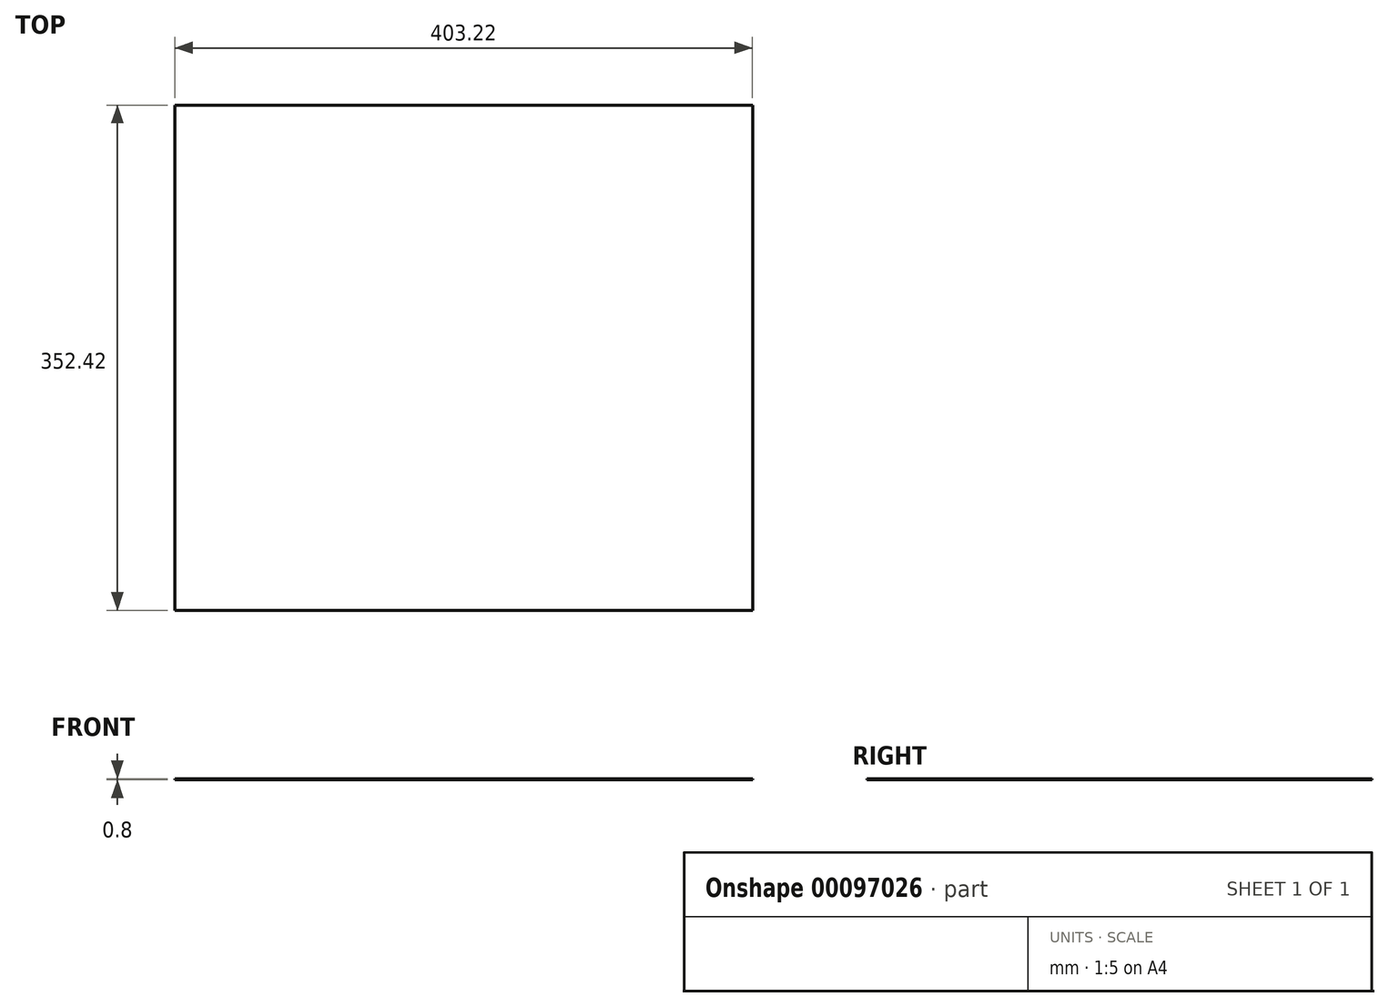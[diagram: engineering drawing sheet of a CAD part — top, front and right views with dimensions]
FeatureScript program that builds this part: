
annotation { "Feature Type Name" : "Feature", "Feature Type Description" : "" }
export const myFeature = defineFeature(function(context is Context, id is Id, definition is map)
    precondition{}
    {
        {
            var Q0;
            Q0=qCreatedBy(makeId("Top.planeOp"),FACE);
            var sketch = newSketch(context, id + "F0", { "sketchPlane" : qUnion([Q0])});
            skLineSegment(sketch, "E0.bottom", {"start": v(-201.61, 176.21) * mm, "end": v(201.61, 176.21) * mm});
            skLineSegment(sketch, "E0.top", {"start": v(-201.61, -176.21) * mm, "end": v(201.61, -176.21) * mm});
            skLineSegment(sketch, "E0.left", {"start": v(-201.61, 176.21) * mm, "end": v(-201.61, -176.21) * mm});
            skLineSegment(sketch, "E0.right", {"start": v(201.61, 176.21) * mm, "end": v(201.61, -176.21) * mm});
            skPoint(sketch, "E0.middle", {"position": v(0, 0) * mm});
            skSolve(sketch);
        }
        {
            var Q0;
            Q0=makeQuery(id+"F0.imprint","IMPRINT",FACE,{"disambiguationData":[TD([[makeQuery(id+"F0.imprint","IMPRINT",EDGE,{"derivedFrom":sQuery(id+"F0.wireOp",EDGE,"E0.bottom")}),-1.0]])]});
            extrude(context, id + "F1", {"entities" : qUnion([Q0]), "endBound" : BoundingType.SYMMETRIC, "depth" : 0.8 * mm});
        }
    });
